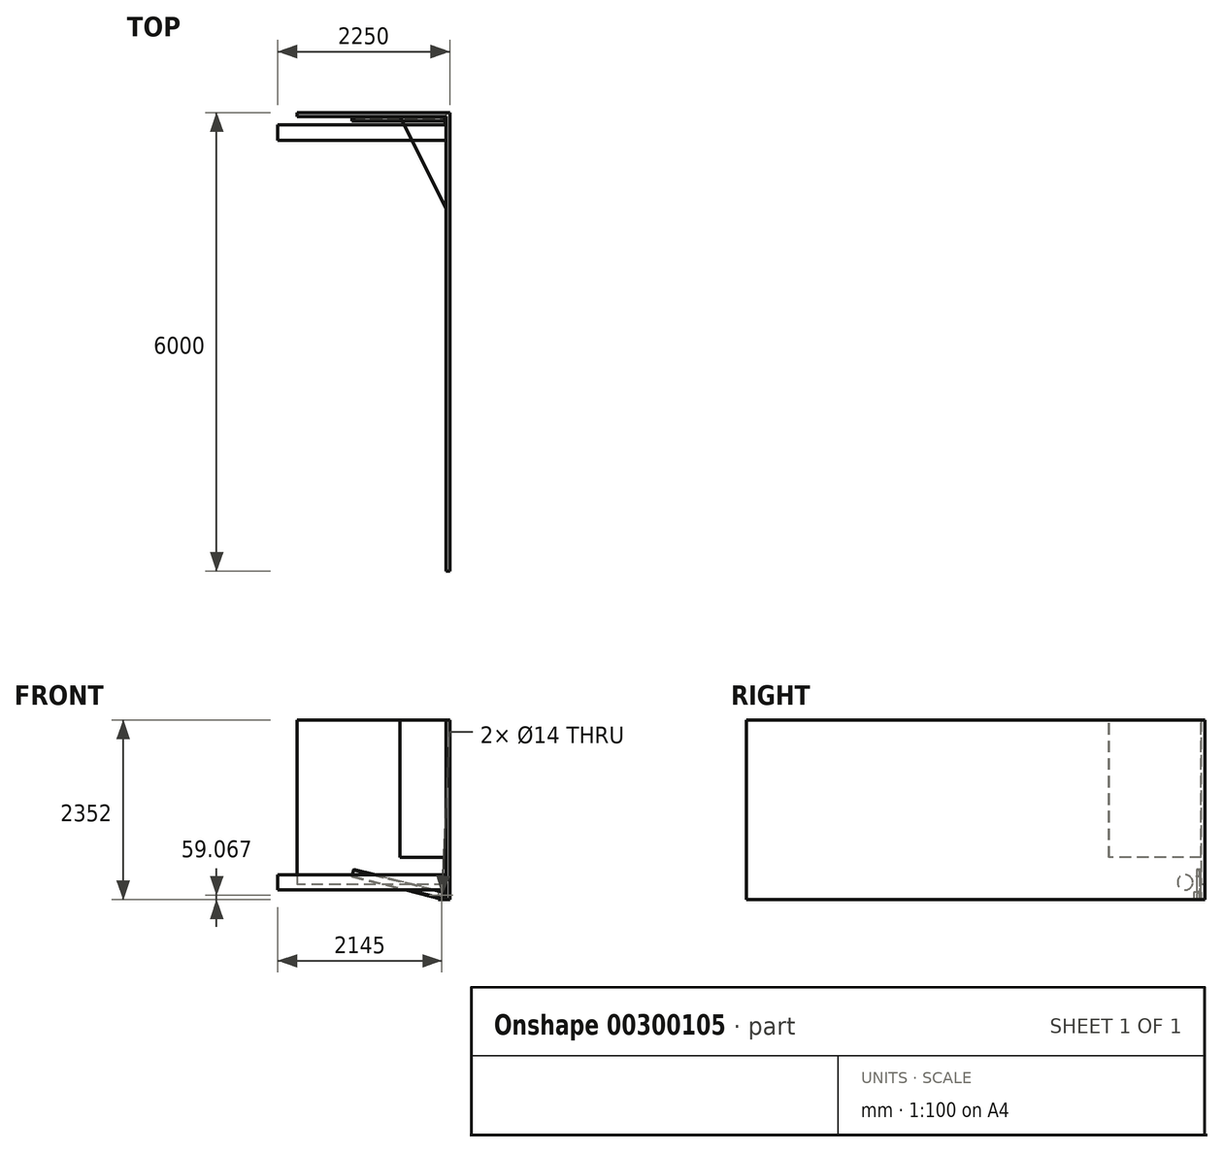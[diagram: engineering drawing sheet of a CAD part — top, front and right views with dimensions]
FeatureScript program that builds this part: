
annotation { "Feature Type Name" : "Feature", "Feature Type Description" : "" }
export const myFeature = defineFeature(function(context is Context, id is Id, definition is map)
    precondition{}
    {
        {
            var Q0;
            Q0=qCreatedBy(makeId("Top.planeOp"),FACE);
            var sketch = newSketch(context, id + "F0", { "sketchPlane" : qUnion([Q0])});
            skLineSegment(sketch, "E0.bottom", {"start": v(0, 0) * mm, "end": v(2000, 0) * mm});
            skLineSegment(sketch, "E0.top", {"start": v(0, -50) * mm, "end": v(2000, -50) * mm});
            skLineSegment(sketch, "E0.left", {"start": v(0, 0) * mm, "end": v(0, -50) * mm});
            skLineSegment(sketch, "E0.right", {"start": v(2000, 0) * mm, "end": v(2000, -50) * mm});
            skLineSegment(sketch, "E1.bottom", {"start": v(2000, 0) * mm, "end": v(1950, 0) * mm});
            skLineSegment(sketch, "E1.top", {"start": v(2000, -6000) * mm, "end": v(1950, -6000) * mm});
            skLineSegment(sketch, "E1.left", {"start": v(2000, 0) * mm, "end": v(2000, -6000) * mm});
            skLineSegment(sketch, "E1.right", {"start": v(1950, 0) * mm, "end": v(1950, -6000) * mm});
            skSolve(sketch);
        }
        {
            var Q0;
            Q0 = qSketchRegion(id + "F0", true);
            extrude(context, id + "F1", {"entities" : qUnion([Q0]), "depth" : 2352 * mm});
        }
        {
            var Q0;
            Q0=makeQuery(id+"F1.opExtrude","SWEPT_FACE",FACE,{"disambiguationData":[OSD([sQuery(id+"F0.wireOp",EDGE,"E1.right")])]});
            var sketch = newSketch(context, id + "F2", { "sketchPlane" : qUnion([Q0])});
            skPoint(sketch, "E2", {"position": v(260, 227) * mm});
            skCircle(sketch, "E3", {"center": v(260, 227) * mm, "radius": 50 * mm});
            skCircle(sketch, "E4", {"center": v(260, 227) * mm, "radius": 100 * mm});
            skSolve(sketch);
        }
        {
            var Q0;
            Q0=makeQuery(id+"F2.imprint","IMPRINT",FACE,{"disambiguationData":[TD([[makeQuery(id+"F2.imprint","IMPRINT",EDGE,{"derivedFrom":sQuery(id+"F2.wireOp",EDGE,"E3")}),1.0]])]});
            var Q1;
            Q1=makeQuery(id+"F2.imprint","IMPRINT",FACE,{"disambiguationData":[TD([[makeQuery(id+"F2.imprint","IMPRINT",EDGE,{"derivedFrom":sQuery(id+"F2.wireOp",EDGE,"E3")}),-1.0]])]});
            extrude(context, id + "F3", {"entities" : qUnion([Q0, Q1]), "depth" : 2200 * mm});
        }
        {
            var Q0;
            Q0=makeQuery(id+"F1.opExtrude","CAP_FACE",FACE,{"disambiguationData":[OSD([sQuery(id+"F0.wireOp",EDGE,"E0.bottom"),sQuery(id+"F0.wireOp",EDGE,"E0.top"),sQuery(id+"F0.wireOp",EDGE,"E0.left"),sQuery(id+"F0.wireOp",EDGE,"E1.bottom"),sQuery(id+"F0.wireOp",EDGE,"E1.top"),sQuery(id+"F0.wireOp",EDGE,"E1.left"),sQuery(id+"F0.wireOp",EDGE,"E1.right")])],"isStart":false});
            var sketch = newSketch(context, id + "F4", { "sketchPlane" : qUnion([Q0])});
            skLineSegment(sketch, "E5.0", {"start": v(0, -50) * mm, "end": v(1950, -50) * mm});
            skLineSegment(sketch, "E5.1", {"start": v(1950, -50) * mm, "end": v(1950, -6000) * mm});
            skLineSegment(sketch, "E6", {"start": v(1350, -50) * mm, "end": v(1950, -1250) * mm});
            skLineSegment(sketch, "E7.0", {"start": v(1345.53, -50) * mm, "end": v(1950, -1258.94) * mm});
            skSolve(sketch);
        }
        {
            var Q0;
            {var subQ0=sQuery(id+"F4.wireOp",EDGE,"E6");Q0=makeQuery(id+"F4.imprint","IMPRINT",FACE,{"disambiguationData":[TD([[makeQuery(id+"F4.imprint","IMPRINT",EDGE,{"derivedFrom":subQ0}),-1.0]])]});}
            extrude(context, id + "F5", {"entities" : qUnion([Q0]), "oppositeDirection" : true, "depth" : 1800 * mm});
        }
        {
            var Q0;
            Q0=makeQuery(id+"F1.opExtrude","SWEPT_FACE",FACE,{"disambiguationData":[OSD([sQuery(id+"F0.wireOp",EDGE,"E0.top")])]});
            var sketch = newSketch(context, id + "F6", { "sketchPlane" : qUnion([Q0])});
            skLineSegment(sketch, "E8.bottom", {"start": v(1950, 0) * mm, "end": v(0, 0) * mm});
            skLineSegment(sketch, "E8.top", {"start": v(1950, 199.04) * mm, "end": v(0, 199.04) * mm});
            skLineSegment(sketch, "E8.left", {"start": v(1950, 0) * mm, "end": v(1950, 199.04) * mm});
            skLineSegment(sketch, "E8.right", {"start": v(0, 0) * mm, "end": v(0, 199.04) * mm});
            skSolve(sketch);
        }
        {
            var Q0;
            Q0 = qSketchRegion(id + "F6", true);
            extrude(context, id + "F7", {"entities" : qUnion([Q0]), "operationType" : NewBodyOperationType.REMOVE, "endBound" : BoundingType.THROUGH_ALL, "oppositeDirection" : true, "depth" : 25 * mm});
        }
        {
            var Q0;
            Q0=makeQuery(id+"F1.opExtrude","CAP_FACE",FACE,{"disambiguationData":[OSD([sQuery(id+"F0.wireOp",EDGE,"E0.bottom"),sQuery(id+"F0.wireOp",EDGE,"E0.top"),sQuery(id+"F0.wireOp",EDGE,"E0.left"),sQuery(id+"F0.wireOp",EDGE,"E1.bottom"),sQuery(id+"F0.wireOp",EDGE,"E1.top"),sQuery(id+"F0.wireOp",EDGE,"E1.left"),sQuery(id+"F0.wireOp",EDGE,"E1.right")])],"isStart":true});
            var sketch = newSketch(context, id + "F8", { "sketchPlane" : qUnion([Q0])});
            skPoint(sketch, "E9.0", {"position": v(1950, 50) * mm});
            skLineSegment(sketch, "E10.bottom", {"start": v(1950, 50) * mm, "end": v(1850, 50) * mm});
            skLineSegment(sketch, "E10.top", {"start": v(1950, 60) * mm, "end": v(1850, 60) * mm});
            skLineSegment(sketch, "E10.left", {"start": v(1950, 50) * mm, "end": v(1950, 60) * mm});
            skLineSegment(sketch, "E10.right", {"start": v(1850, 50) * mm, "end": v(1850, 60) * mm});
            skLineSegment(sketch, "E11.bottom", {"start": v(1950, 50) * mm, "end": v(1940, 50) * mm});
            skLineSegment(sketch, "E11.top", {"start": v(1950, 150) * mm, "end": v(1940, 150) * mm});
            skLineSegment(sketch, "E11.left", {"start": v(1950, 50) * mm, "end": v(1950, 150) * mm});
            skLineSegment(sketch, "E11.right", {"start": v(1940, 50) * mm, "end": v(1940, 150) * mm});
            skSolve(sketch);
        }
        {
            var Q0;
            Q0 = qSketchRegion(id + "F8", true);
            extrude(context, id + "F9", {"entities" : qUnion([Q0]), "oppositeDirection" : true, "depth" : 100 * mm});
        }
        {
            var Q0;
            Q0=makeQuery(id+"F9.opExtrude","SWEPT_FACE",FACE,{"disambiguationData":[OSD([sQuery(id+"F8.wireOp",EDGE,"E10.top")])]});
            var sketch = newSketch(context, id + "F10", { "sketchPlane" : qUnion([Q0])});
            skPoint(sketch, "E12", {"position": v(1895, 59.07) * mm});
            skPoint(sketch, "E12.positionSnap0", {"position": v(1895, 0) * mm});
            skPoint(sketch, "E12.positionSnap1", {"position": v(1850, 50) * mm});
            skLineSegment(sketch, "E13", {"start": v(1895, 59.07) * mm, "end": v(762.08, 342.1) * mm, "construction": true});
            skLineSegment(sketch, "E14", {"start": v(1895, 59.07) * mm, "end": v(1883.45, 12.83) * mm, "construction": true});
            skSolve(sketch);
        }
        {
            var Q0;
            Q0=sQuery(id+"F10.wireOp",EDGE,"E14");
            cPlane(context, id + "F11", {"entities" : qUnion([Q0]), "cplaneType" : CPlaneType.LINE_ANGLE, "offset" : 25 * mm, "angle" : 0 * degree, "width" : 150 * mm, "height" : 150 * mm});
        }
        {
            var Q0;
            Q0=qCreatedBy(id+"F11.planeOp",FACE);
            var sketch = newSketch(context, id + "F12", { "sketchPlane" : qUnion([Q0])});
            skLineSegment(sketch, "E15.0", {"start": v(60, 545.41) * mm, "end": v(60, 448.4) * mm});
            skPoint(sketch, "E16.0", {"position": v(60, 516.6) * mm});
            skLineSegment(sketch, "E17", {"start": v(117.75, 516.6) * mm, "end": v(-10.66, 516.6) * mm, "construction": true});
            skLineSegment(sketch, "E18", {"start": v(60, 516.6) * mm, "end": v(60, 566.6) * mm});
            skLineSegment(sketch, "E19", {"start": v(60, 566.6) * mm, "end": v(110, 566.6) * mm});
            skLineSegment(sketch, "E20", {"start": v(110, 566.6) * mm, "end": v(110, 556.6) * mm});
            skLineSegment(sketch, "E21", {"start": v(110, 556.6) * mm, "end": v(80, 556.6) * mm});
            skLineSegment(sketch, "E22", {"start": v(70, 546.6) * mm, "end": v(70, 516.6) * mm});
            skPoint(sketch, "E23.visualSharp", {"position": v(70, 556.6) * mm});
            skArc(sketch, "E23.filletArc", {"start": v(80, 556.6) * mm, "mid": v(72.93, 553.68) * mm, "end": v(70, 546.6) * mm});
            skLineSegment(sketch, "E24.MirrorCS", {"start": v(70, 486.6) * mm, "end": v(70, 516.6) * mm});
            skArc(sketch, "E25.MirrorCS", {"start": v(80, 476.6) * mm, "mid": v(72.93, 479.53) * mm, "end": v(70, 486.6) * mm});
            skLineSegment(sketch, "E26.MirrorCS", {"start": v(110, 476.6) * mm, "end": v(80, 476.6) * mm});
            skLineSegment(sketch, "E27.MirrorCS", {"start": v(110, 466.6) * mm, "end": v(110, 476.6) * mm});
            skLineSegment(sketch, "E28.MirrorCS", {"start": v(60, 466.6) * mm, "end": v(110, 466.6) * mm});
            skLineSegment(sketch, "E29.MirrorCS", {"start": v(60, 516.6) * mm, "end": v(60, 466.6) * mm});
            skSolve(sketch);
        }
        {
            var Q0;
            Q0 = qSketchRegion(id + "F12", true);
            extrude(context, id + "F13", {"entities" : qUnion([Q0]), "depth" : 1200 * mm, "hasSecondDirection" : true, "secondDirectionOppositeDirection" : true, "secondDirectionDepth" : 25 * mm});
        }
        {
            var Q0;
            Q0=sQuery(id+"F10.wireOp",VERTEX,"E12");
            var Q1;
            Q1=makeQuery(id+"F13.opExtrude","SWEPT_BODY",BODY,{"disambiguationData":[OSD([sQuery(id+"F12.wireOp",EDGE,"E18"),sQuery(id+"F12.wireOp",EDGE,"E19"),sQuery(id+"F12.wireOp",EDGE,"E20"),sQuery(id+"F12.wireOp",EDGE,"E21"),sQuery(id+"F12.wireOp",EDGE,"E22"),sQuery(id+"F12.wireOp",EDGE,"E23.filletArc"),sQuery(id+"F12.wireOp",EDGE,"E24.MirrorCS"),sQuery(id+"F12.wireOp",EDGE,"E25.MirrorCS"),sQuery(id+"F12.wireOp",EDGE,"E26.MirrorCS"),sQuery(id+"F12.wireOp",EDGE,"E27.MirrorCS"),sQuery(id+"F12.wireOp",EDGE,"E28.MirrorCS"),sQuery(id+"F12.wireOp",EDGE,"E29.MirrorCS")])]});
            hole(context, id + "F14", {"style" : HoleStyle.SIMPLE, "endStyle" : HoleEndStyle.BLIND, "oppositeDirection" : true, "standardTappedOrClearance" : lookupTablePath({ "standard" : "ISO", "engagement" : "75%", "pitch" : "2 mm", "size" : "M16", "type" : "Tapped" }), "standardBlindInLast" : lookupTablePath({ "standard" : "ISO", "engagement" : "75%", "pitch" : "2 mm", "size" : "M16", "type" : "Tapped" }), "holeDiameter" : 14 * mm, "showTappedDepth" : true, "holeDepth" : 12.75 * mm, "tappedDepth" : 6.75 * mm, "tapClearance" : 3, "locations" : qUnion([Q0]), "scope" : qUnion([Q1]), "majorDiameter" : 16 * mm});
        }
        {
            var Q0;
            Q0=sQuery(id+"F10.wireOp",VERTEX,"E12");
            var Q1;
            Q1=makeQuery(id+"F9.opExtrude","SWEPT_BODY",BODY,{"disambiguationData":[OSD([sQuery(id+"F8.wireOp",EDGE,"E10.bottom"),sQuery(id+"F8.wireOp",EDGE,"E10.top"),sQuery(id+"F8.wireOp",EDGE,"E10.right"),sQuery(id+"F8.wireOp",EDGE,"E11.bottom"),sQuery(id+"F8.wireOp",EDGE,"E11.top"),sQuery(id+"F8.wireOp",EDGE,"E11.left"),sQuery(id+"F8.wireOp",EDGE,"E11.right")])]});
            hole(context, id + "F15", {"style" : HoleStyle.SIMPLE, "endStyle" : HoleEndStyle.BLIND, "standardTappedOrClearance" : lookupTablePath({ "standard" : "ISO", "engagement" : "75%", "pitch" : "2 mm", "size" : "M16", "type" : "Tapped" }), "standardBlindInLast" : lookupTablePath({ "standard" : "ISO", "engagement" : "75%", "pitch" : "2 mm", "size" : "M16", "type" : "Tapped" }), "holeDiameter" : 14 * mm, "showTappedDepth" : true, "holeDepth" : 12.75 * mm, "tappedDepth" : 6.75 * mm, "tapClearance" : 3, "locations" : qUnion([Q0]), "scope" : qUnion([Q1]), "majorDiameter" : 16 * mm});
        }
    });
